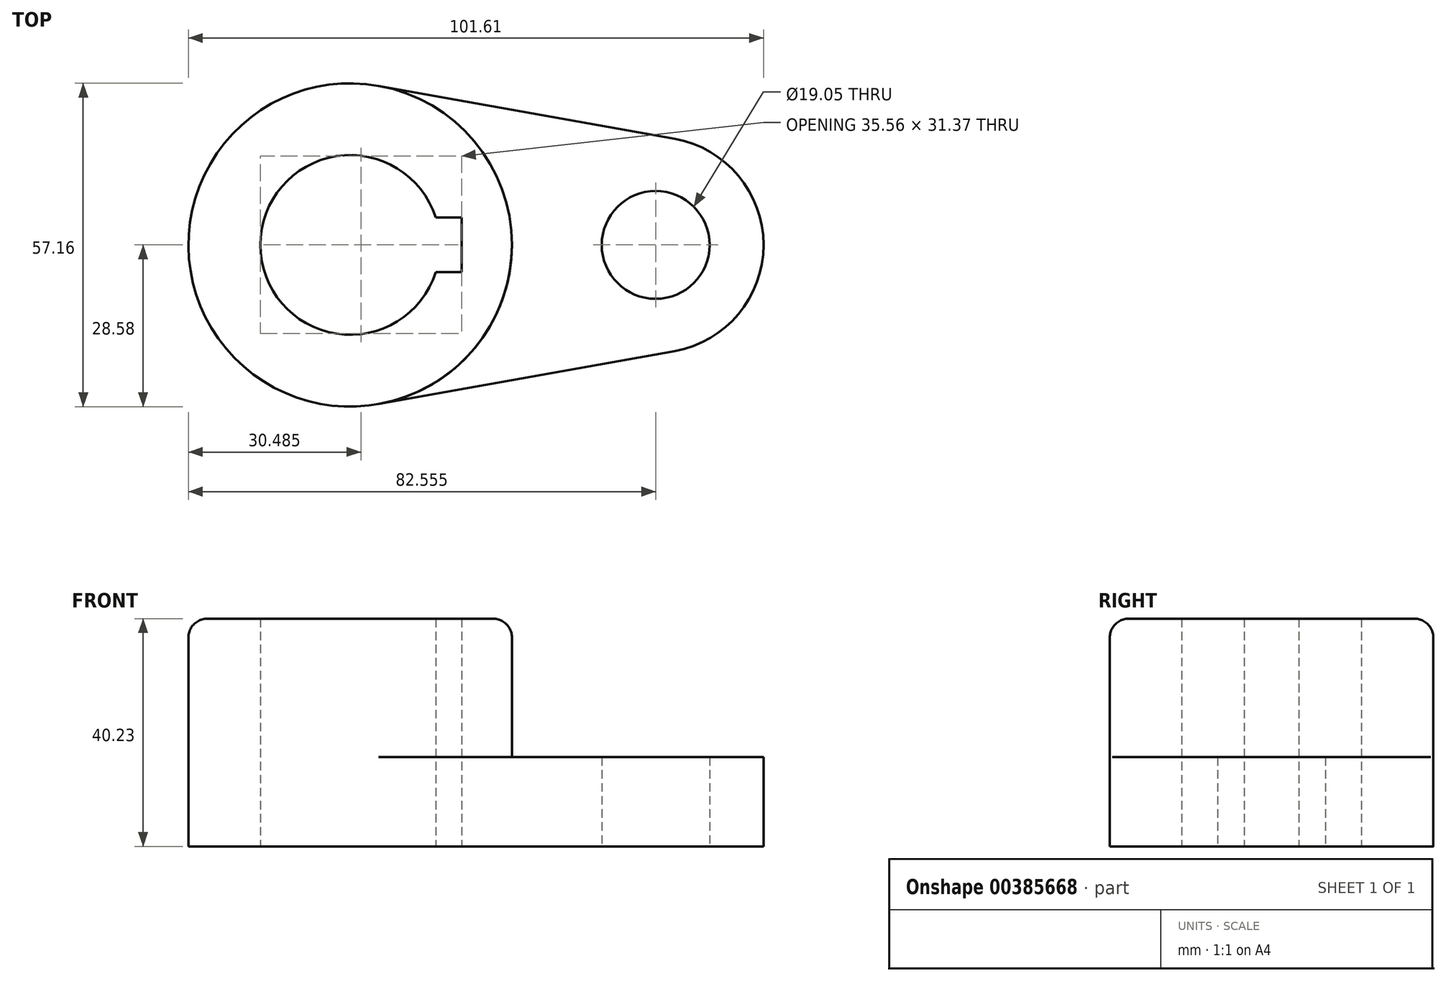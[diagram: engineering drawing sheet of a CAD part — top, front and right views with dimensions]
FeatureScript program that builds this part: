
annotation { "Feature Type Name" : "Feature", "Feature Type Description" : "" }
export const myFeature = defineFeature(function(context is Context, id is Id, definition is map)
    precondition{}
    {
        {
            var Q0;
            Q0=qCreatedBy(makeId("Top.planeOp"),FACE);
            var sketch = newSketch(context, id + "F0", { "sketchPlane" : qUnion([Q0])});
            skCircle(sketch, "E0", {"center": v(0, 0) * mm, "radius": 15.88 * mm});
            skCircle(sketch, "E1", {"center": v(0, 0) * mm, "radius": 28.57 * mm});
            skCircle(sketch, "E2", {"center": v(53.98, 0) * mm, "radius": 9.53 * mm});
            skCircle(sketch, "E3", {"center": v(53.98, 0) * mm, "radius": 19.05 * mm});
            skLineSegment(sketch, "E4", {"start": v(5.04, 28.13) * mm, "end": v(57.34, 18.75) * mm});
            skLineSegment(sketch, "E5", {"start": v(5.04, -28.13) * mm, "end": v(57.34, -18.75) * mm});
            skLineSegment(sketch, "E6", {"start": v(15.12, -4.83) * mm, "end": v(19.69, -4.83) * mm});
            skLineSegment(sketch, "E7", {"start": v(19.69, -4.83) * mm, "end": v(19.69, 4.83) * mm});
            skLineSegment(sketch, "E8", {"start": v(19.69, 4.83) * mm, "end": v(15.12, 4.83) * mm});
            skLineSegment(sketch, "E9", {"start": v(0, 0) * mm, "end": v(100.21, 0) * mm, "construction": true});
            skSolve(sketch);
        }
        {
            var Q0;
            {var subQ0=sQuery(id+"F0.wireOp",EDGE,"E6");Q0=makeQuery(id+"F0.imprint","IMPRINT",FACE,{"disambiguationData":[TD([[makeQuery(id+"F0.imprint","IMPRINT",EDGE,{"derivedFrom":subQ0}),-1.0]])]});}
            extrude(context, id + "F1", {"entities" : qUnion([Q0]), "depth" : 40.23 * mm});
        }
        {
            var Q0;
            {var subQ0=sQuery(id+"F0.wireOp",EDGE,"E4");Q0=makeQuery(id+"F0.imprint","IMPRINT",FACE,{"disambiguationData":[TD([[makeQuery(id+"F0.imprint","IMPRINT",EDGE,{"derivedFrom":subQ0}),-1.0]])]});}
            var Q1;
            Q1=makeQuery(id+"F0.imprint","IMPRINT",FACE,{"disambiguationData":[TD([[makeQuery(id+"F0.imprint","IMPRINT",EDGE,{"derivedFrom":sQuery(id+"F0.wireOp",EDGE,"E2")}),-1.0]])]});
            extrude(context, id + "F2", {"entities" : qUnion([Q0, Q1]), "operationType" : NewBodyOperationType.ADD, "depth" : 15.77 * mm});
        }
        {
            var Q0;
            Q0=makeQuery(id+"F1.opExtrude","CAP_EDGE",EDGE,{"disambiguationData":[OSD([sQuery(id+"F0.wireOp",EDGE,"E1")])],"isStart":false});
            fillet(context, id + "F3", {"entities" : qUnion([Q0]), "radius" : 3.3 * mm, "tangentPropagation" : true, "allowEdgeOverflow" : false});
        }
    });
